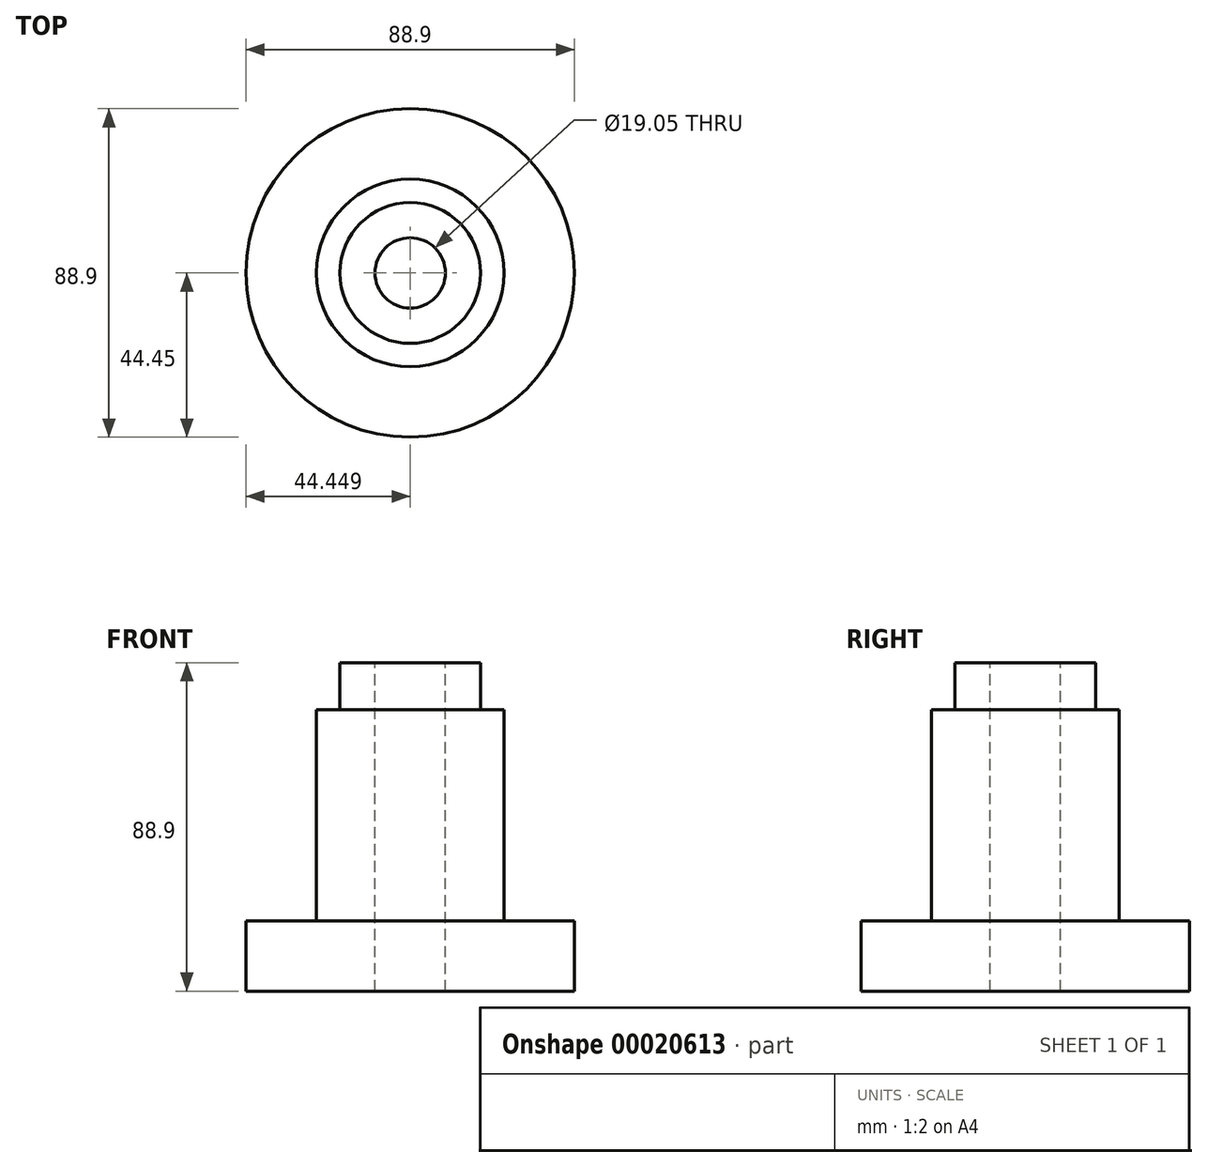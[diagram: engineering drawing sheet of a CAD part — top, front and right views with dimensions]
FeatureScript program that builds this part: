
annotation { "Feature Type Name" : "Feature", "Feature Type Description" : "" }
export const myFeature = defineFeature(function(context is Context, id is Id, definition is map)
    precondition{}
    {
        {
            var Q0;
            Q0=qCreatedBy(makeId("Front.planeOp"),FACE);
            var sketch = newSketch(context, id + "F0", { "sketchPlane" : qUnion([Q0])});
            skLineSegment(sketch, "E0", {"start": v(-59.9, 36.84) * mm, "end": v(-59.9, -52.06) * mm});
            skLineSegment(sketch, "E1", {"start": v(-59.9, -52.06) * mm, "end": v(-24.98, -52.06) * mm});
            skLineSegment(sketch, "E2", {"start": v(-24.98, -52.06) * mm, "end": v(-24.98, -33.01) * mm});
            skLineSegment(sketch, "E3", {"start": v(-24.98, -33.01) * mm, "end": v(-44.03, -33.01) * mm});
            skLineSegment(sketch, "E4", {"start": v(-44.03, -33.01) * mm, "end": v(-44.03, 24.14) * mm});
            skLineSegment(sketch, "E5", {"start": v(-44.03, 24.14) * mm, "end": v(-50.38, 24.14) * mm});
            skLineSegment(sketch, "E6", {"start": v(-50.38, 24.14) * mm, "end": v(-50.38, 36.84) * mm});
            skLineSegment(sketch, "E7", {"start": v(-50.38, 36.84) * mm, "end": v(-59.9, 36.84) * mm});
            skLineSegment(sketch, "E8", {"start": v(-69.43, 36.84) * mm, "end": v(-69.43, -50.8) * mm});
            skSolve(sketch);
        }
        {
            var Q0;
            Q0=makeQuery(id+"F0.imprint","IMPRINT",FACE,{"disambiguationData":[TD([[makeQuery(id+"F0.imprint","IMPRINT",EDGE,{"derivedFrom":sQuery(id+"F0.wireOp",EDGE,"E0")}),1.0]])]});
            var Q1;
            Q1=sQuery(id+"F0.wireOp",EDGE,"E8");
            revolve(context, id + "F1", {"entities" : qUnion([Q0]), "axis" : qUnion([Q1]), "revolveType" : RevolveType.FULL});
        }
    });
